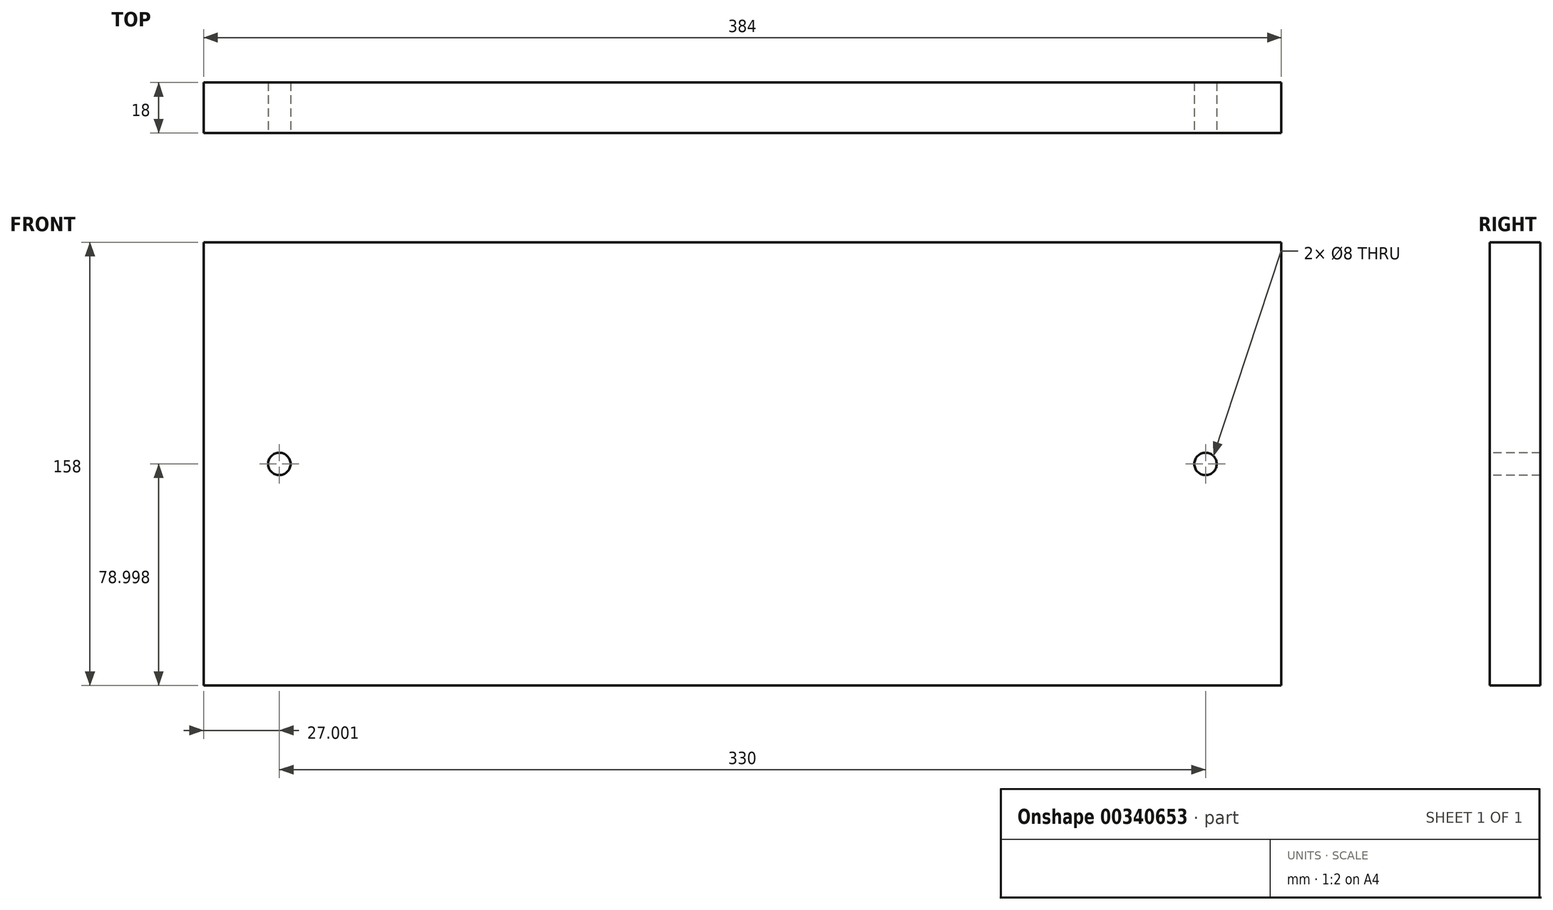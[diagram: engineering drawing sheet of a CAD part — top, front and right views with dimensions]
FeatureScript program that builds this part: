
annotation { "Feature Type Name" : "Feature", "Feature Type Description" : "" }
export const myFeature = defineFeature(function(context is Context, id is Id, definition is map)
    precondition{}
    {
        {
            var Q0;
            Q0=qCreatedBy(makeId("Front.planeOp"),FACE);
            var sketch = newSketch(context, id + "F0", { "sketchPlane" : qUnion([Q0])});
            skLineSegment(sketch, "E0.bottom", {"start": v(-186.7, 104.29) * mm, "end": v(197.3, 104.29) * mm});
            skLineSegment(sketch, "E0.top", {"start": v(-186.7, -53.71) * mm, "end": v(197.3, -53.71) * mm});
            skLineSegment(sketch, "E0.left", {"start": v(-186.7, 104.29) * mm, "end": v(-186.7, -53.71) * mm});
            skLineSegment(sketch, "E0.right", {"start": v(197.3, 104.29) * mm, "end": v(197.3, -53.71) * mm});
            skLineSegment(sketch, "E1", {"start": v(-159.7, 125.61) * mm, "end": v(-159.7, -86.38) * mm, "construction": true});
            skLineSegment(sketch, "E2", {"start": v(-214.47, 25.29) * mm, "end": v(235.8, 25.29) * mm, "construction": true});
            skCircle(sketch, "E3", {"center": v(-159.7, 25.29) * mm, "radius": 4 * mm});
            skLineSegment(sketch, "E4", {"start": v(170.3, 124.02) * mm, "end": v(170.3, -77.83) * mm, "construction": true});
            skCircle(sketch, "E5", {"center": v(170.3, 25.29) * mm, "radius": 4 * mm});
            skSolve(sketch);
        }
        {
            var Q0;
            Q0=makeQuery(id+"F0.imprint","IMPRINT",FACE,{"disambiguationData":[TD([[makeQuery(id+"F0.imprint","IMPRINT",EDGE,{"derivedFrom":sQuery(id+"F0.wireOp",EDGE,"E0.bottom")}),-1.0]])]});
            extrude(context, id + "F1", {"entities" : qUnion([Q0]), "oppositeDirection" : true, "depth" : 18 * mm});
        }
    });
